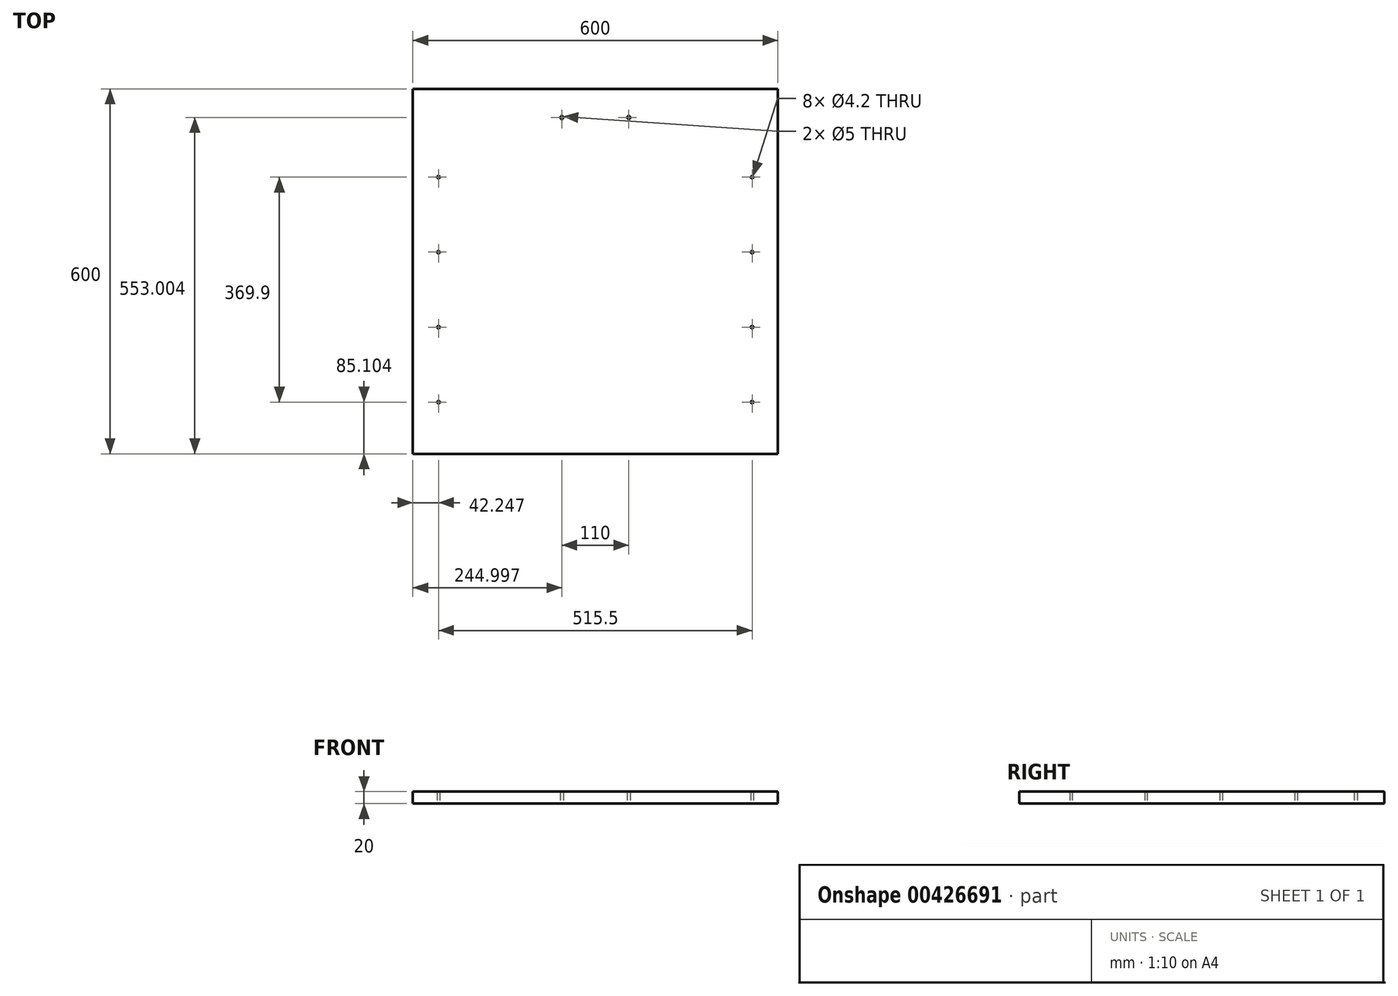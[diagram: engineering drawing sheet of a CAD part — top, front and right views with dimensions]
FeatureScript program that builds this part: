
annotation { "Feature Type Name" : "Feature", "Feature Type Description" : "" }
export const myFeature = defineFeature(function(context is Context, id is Id, definition is map)
    precondition{}
    {
        {
            var Q0;
            Q0=qCreatedBy(makeId("Top.planeOp"),FACE);
            var sketch = newSketch(context, id + "F0", { "sketchPlane" : qUnion([Q0])});
            skLineSegment(sketch, "E0.bottom", {"start": v(-722.9, 558) * mm, "end": v(-122.9, 558) * mm});
            skLineSegment(sketch, "E0.top", {"start": v(-722.9, -42) * mm, "end": v(-122.9, -42) * mm});
            skLineSegment(sketch, "E0.left", {"start": v(-722.9, 558) * mm, "end": v(-722.9, -42) * mm});
            skLineSegment(sketch, "E0.right", {"start": v(-122.9, 558) * mm, "end": v(-122.9, -42) * mm});
            skLineSegment(sketch, "E1.0", {"start": v(-422.9, 521) * mm, "end": v(-422.9, -42) * mm});
            skPoint(sketch, "E2", {"position": v(-477.9, 511) * mm});
            skPoint(sketch, "E3", {"position": v(-367.9, 511) * mm});
            skPoint(sketch, "E4", {"position": v(-680.64, 413) * mm});
            skPoint(sketch, "E5", {"position": v(-680.64, 289.7) * mm});
            skPoint(sketch, "E6", {"position": v(-680.64, 166.4) * mm});
            skPoint(sketch, "E7", {"position": v(-680.64, 43.1) * mm});
            skPoint(sketch, "E8", {"position": v(-165.14, 413) * mm});
            skPoint(sketch, "E9", {"position": v(-165.14, 289.7) * mm});
            skPoint(sketch, "E10", {"position": v(-165.14, 166.4) * mm});
            skPoint(sketch, "E11", {"position": v(-165.14, 43.1) * mm});
            skPoint(sketch, "E12", {"position": v(-662.9, 518) * mm});
            skPoint(sketch, "E13", {"position": v(-626.9, 518) * mm});
            skPoint(sketch, "E14", {"position": v(-626.9, 486) * mm});
            skPoint(sketch, "E15", {"position": v(-662.9, 486) * mm});
            skPoint(sketch, "E16", {"position": v(-218.9, 518) * mm});
            skPoint(sketch, "E17", {"position": v(-182.9, 518) * mm});
            skPoint(sketch, "E18", {"position": v(-182.9, 486) * mm});
            skPoint(sketch, "E19", {"position": v(-218.9, 486) * mm});
            skSolve(sketch);
        }
        {
            var Q0;
            {var subQ0=sQuery(id+"F0.wireOp",EDGE,"E0.left");Q0=makeQuery(id+"F0.imprint","IMPRINT",FACE,{"disambiguationData":[TD([[makeQuery(id+"F0.imprint","IMPRINT",EDGE,{"derivedFrom":subQ0}),1.0]])]});}
            var Q1;
            {var subQ0=sQuery(id+"F0.wireOp",EDGE,"E0.right");Q1=makeQuery(id+"F0.imprint","IMPRINT",FACE,{"disambiguationData":[TD([[makeQuery(id+"F0.imprint","IMPRINT",EDGE,{"derivedFrom":subQ0}),-1.0]])]});}
            extrude(context, id + "F1", {"entities" : qUnion([Q0, Q1]), "depth" : 20 * mm});
        }
        {
            var Q0;
            Q0=sQuery(id+"F0.wireOp",VERTEX,"E2");
            var Q1;
            Q1=sQuery(id+"F0.wireOp",VERTEX,"E3");
            var Q2;
            Q2=makeQuery(id+"F1.opExtrude","SWEPT_BODY",BODY,{"disambiguationData":[OSD([sQuery(id+"F0.wireOp",EDGE,"E0.bottom"),sQuery(id+"F0.wireOp",EDGE,"E0.top"),sQuery(id+"F0.wireOp",EDGE,"E0.left"),sQuery(id+"F0.wireOp",EDGE,"E0.right")])]});
            hole(context, id + "F2", {"style" : HoleStyle.SIMPLE, "endStyle" : HoleEndStyle.THROUGH, "oppositeDirection" : true, "standardTappedOrClearance" : lookupTablePath({ "standard" : "ISO", "engagement" : "75%", "pitch" : "1 mm", "size" : "M6", "type" : "Tapped" }), "standardBlindInLast" : lookupTablePath({ "standard" : "ISO", "engagement" : "75%", "pitch" : "1 mm", "size" : "M6", "type" : "Tapped" }), "holeDiameter" : 5 * mm, "showTappedDepth" : true, "isTappedThrough" : true, "tappedDepth" : 10 * mm, "tapClearance" : 3, "locations" : qUnion([Q0, Q1]), "scope" : qUnion([Q2]), "majorDiameter" : 6 * mm});
        }
        {
            var Q0;
            Q0=sQuery(id+"F0.wireOp",VERTEX,"E4");
            var Q1;
            Q1=sQuery(id+"F0.wireOp",VERTEX,"E5");
            var Q2;
            Q2=sQuery(id+"F0.wireOp",VERTEX,"E6");
            var Q3;
            Q3=sQuery(id+"F0.wireOp",VERTEX,"E7");
            var Q4;
            Q4=sQuery(id+"F0.wireOp",VERTEX,"E11");
            var Q5;
            Q5=sQuery(id+"F0.wireOp",VERTEX,"E10");
            var Q6;
            Q6=sQuery(id+"F0.wireOp",VERTEX,"E9");
            var Q7;
            Q7=sQuery(id+"F0.wireOp",VERTEX,"E8");
            var Q8;
            Q8=makeQuery(id+"F1.opExtrude","SWEPT_BODY",BODY,{"disambiguationData":[OSD([sQuery(id+"F0.wireOp",EDGE,"E0.bottom"),sQuery(id+"F0.wireOp",EDGE,"E0.top"),sQuery(id+"F0.wireOp",EDGE,"E0.left"),sQuery(id+"F0.wireOp",EDGE,"E0.right")])]});
            hole(context, id + "F3", {"style" : HoleStyle.SIMPLE, "endStyle" : HoleEndStyle.THROUGH, "oppositeDirection" : true, "standardTappedOrClearance" : lookupTablePath({ "standard" : "ISO", "engagement" : "75%", "pitch" : "0.8 mm", "size" : "M5", "type" : "Tapped" }), "standardBlindInLast" : lookupTablePath({ "standard" : "ISO", "engagement" : "75%", "pitch" : "0.8 mm", "size" : "M5", "type" : "Tapped" }), "holeDiameter" : 4.2 * mm, "showTappedDepth" : true, "isTappedThrough" : true, "tappedDepth" : 10 * mm, "tapClearance" : 3, "locations" : qUnion([Q0, Q1, Q2, Q3, Q4, Q5, Q6, Q7]), "scope" : qUnion([Q8]), "majorDiameter" : 5 * mm});
        }
    });
